# Revit family: Lighting_Pendant-Lighting_Molto-Luce_Log-Out-2-1-Bina-Lens-Recessed_999
name_source: partatom
category: Lighting Fixtures
revit_build: Autodesk Revit 2018 (Build: 20170223_1515(x64)
units: mm (PartAtom-declared; Revit-internal decimal feet)

## family parameters
Cut with Voids When Loaded = No
Host = Face
Light Source = Yes
OmniClass Number = 23.80.70.00
OmniClass Title = Lighting
Part Type = Normal
Room Calculation Point = No
Round Connector Dimension = Use Diameter
Shared = No

## types (54) — shared parameters
BIMobject category = Pendant Lighting
Color Filter = 16777215
Default Elevation = 1219 mm
Design country = Austria
Dimming Lamp Color Temperature Shift = <None>
Edition number = 1
IFC Classification = Lamp
Installation instructions = https://www.moltoluce.com
Light Source Symbol Size = 610 mm
Manufacturer = Molto Luce
Manufacturer country = Austria
Manufacturer name = Molto Luce
Masterformat 2014 Code = 26 50 00
Masterformat 2014 Description = Lighting
Material main = Aluminium
Material secondary = Acrylic
Model = Log Out 2.1 Bina Lens Recessed
NBS Reference Code = 49
NBS Reference Description = Luminaires And Lamps
OmniClass Code = 23-35 45 15
OmniClass Description = Lamps
Product Guid = 61130c55-a570-4c15-9c05-078dfd1a0b47
Product SKU = Log_Out_2_1_Bina_Lens_Recessed
Product data url = https://bimobject.com
Product family = Lighting
Product group = Pendant Lamp
Product name = Log Out 2.1 Bina Lens Recessed
Product url = https://www.moltoluce.com
QR code = https://bimobject.com
UNSPSC Code = 3911
URL = https://www.moltoluce.com
Uniclass 1.4 Code = JY73
Uniclass 1.4 Description = Luminaires and lamps
Uniclass 2.0 Code = PR-49
Uniclass 2.0 Description = Luminaires And Lamps
Uniclass 2015 Code = Pr_70_70_48
Uniclass 2015 Name = Luminaires, lighting track and lighting accessories
Uniformat II Code = D5020
Uniformat II Description = Lighting & Branch Wiring

## per-type parameters (varying)
| type | Description | Emit from Line Length | Housing Color | Length 1131 mm | Length 2255 mm | Length 3379 mm | Light Location |
| Length 1131 mm 43W - CRI > 80 - Color temperature 4000K - Housing Color Natural Anodised - DALI | LOG OUT 2.1 & LOG IN 2.1 are available as pendant, surface-mounted and recessed luminaires. The profile is made of extruded aluminium and is available in black, white and aluminium-coloured surfaces. Due to its simple, straightforward look, the LOG series can be integrated discretely, yet distinctively into any style of architecture as a great lighting solution. The modular system offers additional components which can be perfectly combined with the profile. The lighting inserts with opal cover or microprismatic foil as well as the new BINA inserts which are available as UGR<19 and as ball-proof version, are just perfect as basic lighting. The Trigga insert and the MOVA spotlight can be used as additional lighting elements for the LOG OUT 2.1, LOG IN 2.1 & LOG IN TRIMLESS 2.1 system. | 1131 mm  [stored 3.71063 ft] | Molto Luce - Natural Anodised | Yes | No | No | 524 mm |
| Length 3379 mm 129W - CRI > 80 - Color temperature 4000K - Housing Color Natural Anodised - DALI |  | 3379 mm  [stored 11.086 ft] | Molto Luce - Natural Anodised | No | No | Yes | 1648 mm |
| Length 2255 mm 86W - CRI > 80 - Color temperature 4000K - Housing Color Natural Anodised - DALI |  | 2255 mm  [stored 7.39829 ft] | Molto Luce - Natural Anodised | No | Yes | No | 1086 mm |
| Length 1131 mm 43W - CRI > 80 - Color temperature 3000K - Housing Color Natural Anodised - DALI |  | 1131 mm  [stored 3.71063 ft] | Molto Luce - Natural Anodised | Yes | No | No | 524 mm |
| Length 3379 mm 129W - CRI > 80 - Color temperature 3000K - Housing Color Natural Anodised - DALI |  | 3379 mm  [stored 11.086 ft] | Molto Luce - Natural Anodised | No | No | Yes | 1648 mm |
| Length 2255 mm 86W - CRI > 80 - Color temperature 3000K - Housing Color Natural Anodised - DALI |  | 2255 mm  [stored 7.39829 ft] | Molto Luce - Natural Anodised | No | Yes | No | 1086 mm |
| Length 1131 mm 43W - CRI > 80 - Color temperature 2700K - Housing Color Natural Anodised - DALI |  | 1131 mm  [stored 3.71063 ft] | Molto Luce - Natural Anodised | Yes | No | No | 524 mm |
| Length 3379 mm 129W - CRI > 80 - Color temperature 2700K - Housing Color Natural Anodised - DALI |  | 3379 mm  [stored 11.086 ft] | Molto Luce - Natural Anodised | No | No | Yes | 1648 mm |
| Length 2255 mm 86W - CRI > 80 - Color temperature 2700K - Housing Color Natural Anodised - DALI |  | 2255 mm  [stored 7.39829 ft] | Molto Luce - Natural Anodised | No | Yes | No | 1086 mm |
| Length 1131 mm 43W - CRI > 80 - Color temperature 4000K - Housing Color White - DALI |  | 1131 mm  [stored 3.71063 ft] | Molto Luce - White | Yes | No | No | 524 mm |
| Length 3379 mm 129W - CRI > 80 - Color temperature 4000K - Housing Color White - DALI |  | 3379 mm  [stored 11.086 ft] | Molto Luce - White | No | No | Yes | 1648 mm |
| Length 2255 mm 86W - CRI > 80 - Color temperature 4000K - Housing Color White - DALI |  | 2255 mm  [stored 7.39829 ft] | Molto Luce - White | No | Yes | No | 1086 mm |
| Length 1131 mm 43W - CRI > 80 - Color temperature 3000K - Housing Color White - DALI |  | 1131 mm  [stored 3.71063 ft] | Molto Luce - White | Yes | No | No | 524 mm |
| Length 3379 mm 129W - CRI > 80 - Color temperature 3000K - Housing Color White - DALI |  | 3379 mm  [stored 11.086 ft] | Molto Luce - White | No | No | Yes | 1648 mm |
| Length 2255 mm 86W - CRI > 80 - Color temperature 3000K - Housing Color White - DALI |  | 2255 mm  [stored 7.39829 ft] | Molto Luce - White | No | Yes | No | 1086 mm |
| Length 1131 mm 43W - CRI > 80 - Color temperature 2700K - Housing Color White - DALI |  | 1131 mm  [stored 3.71063 ft] | Molto Luce - White | Yes | No | No | 524 mm |
| Length 3379 mm 129W - CRI > 80 - Color temperature 2700K - Housing Color White - DALI |  | 3379 mm  [stored 11.086 ft] | Molto Luce - White | No | No | Yes | 1648 mm |
| Length 2255 mm 86W - CRI > 80 - Color temperature 2700K - Housing Color White - DALI |  | 2255 mm  [stored 7.39829 ft] | Molto Luce - White | No | Yes | No | 1086 mm |
| Length 1131 mm 43W - CRI > 80 - Color temperature 4000K - Housing Color Black - DALI |  | 1131 mm  [stored 3.71063 ft] | Molto Luce - Black | Yes | No | No | 524 mm |
| Length 3379 mm 129W - CRI > 80 - Color temperature 4000K - Housing Color Black - DALI |  | 3379 mm  [stored 11.086 ft] | Molto Luce - Black | No | No | Yes | 1648 mm |
| Length 2255 mm 86W - CRI > 80 - Color temperature 4000K - Housing Color Black - DALI |  | 2255 mm  [stored 7.39829 ft] | Molto Luce - Black | No | Yes | No | 1086 mm |
| Length 1131 mm 43W - CRI > 80 - Color temperature 3000K - Housing Color Black - DALI |  | 1131 mm  [stored 3.71063 ft] | Molto Luce - Black | Yes | No | No | 524 mm |
| Length 3379 mm 129W - CRI > 80 - Color temperature 3000K - Housing Color Black - DALI |  | 3379 mm  [stored 11.086 ft] | Molto Luce - Black | No | No | Yes | 1648 mm |
| Length 2255 mm 86W - CRI > 80 - Color temperature 3000K - Housing Color Black - DALI |  | 2255 mm  [stored 7.39829 ft] | Molto Luce - Black | No | Yes | No | 1086 mm |
| Length 1131 mm 43W - CRI > 80 - Color temperature 2700K - Housing Color Black - DALI |  | 1131 mm  [stored 3.71063 ft] | Molto Luce - Black | Yes | No | No | 524 mm |
| Length 3379 mm 129W - CRI > 80 - Color temperature 2700K - Housing Color Black - DALI |  | 3379 mm  [stored 11.086 ft] | Molto Luce - Black | No | No | Yes | 1648 mm |
| Length 2255 mm 86W - CRI > 80 - Color temperature 2700K - Housing Color Black - DALI |  | 2255 mm  [stored 7.39829 ft] | Molto Luce - Black | No | Yes | No | 1086 mm |
| Length 1131 mm 43W - CRI > 80 - Color temperature 4000K - Housing Color Natural Anodised |  | 1131 mm  [stored 3.71063 ft] | Molto Luce - Natural Anodised | Yes | No | No | 524 mm |
| Length 3379 mm 129W - CRI > 80 - Color temperature 4000K - Housing Color Natural Anodised |  | 3379 mm  [stored 11.086 ft] | Molto Luce - Natural Anodised | No | No | Yes | 1648 mm |
| Length 2255 mm 86W - CRI > 80 - Color temperature 4000K - Housing Color Natural Anodised |  | 2255 mm  [stored 7.39829 ft] | Molto Luce - Natural Anodised | No | Yes | No | 1086 mm |
| Length 1131 mm 43W - CRI > 80 - Color temperature 3000K - Housing Color Natural Anodised |  | 1131 mm  [stored 3.71063 ft] | Molto Luce - Natural Anodised | Yes | No | No | 524 mm |
| Length 3379 mm 129W - CRI > 80 - Color temperature 3000K - Housing Color Natural Anodised |  | 3379 mm  [stored 11.086 ft] | Molto Luce - Natural Anodised | No | No | Yes | 1648 mm |
| Length 2255 mm 86W - CRI > 80 - Color temperature 3000K - Housing Color Natural Anodised |  | 2255 mm  [stored 7.39829 ft] | Molto Luce - Natural Anodised | No | Yes | No | 1086 mm |
| Length 1131 mm 43W - CRI > 80 - Color temperature 2700K - Housing Color Natural Anodised |  | 1131 mm  [stored 3.71063 ft] | Molto Luce - Natural Anodised | Yes | No | No | 524 mm |
| Length 3379 mm 129W - CRI > 80 - Color temperature 2700K - Housing Color Natural Anodised |  | 3379 mm  [stored 11.086 ft] | Molto Luce - Natural Anodised | No | No | Yes | 1648 mm |
| Length 2255 mm 86W - CRI > 80 - Color temperature 2700K - Housing Color Natural Anodised |  | 2255 mm  [stored 7.39829 ft] | Molto Luce - Natural Anodised | No | Yes | No | 1086 mm |
| Length 1131 mm 43W - CRI > 80 - Color temperature 4000K - Housing Color White |  | 1131 mm  [stored 3.71063 ft] | Molto Luce - White | Yes | No | No | 524 mm |
| Length 3379 mm 129W - CRI > 80 - Color temperature 4000K - Housing Color White |  | 3379 mm  [stored 11.086 ft] | Molto Luce - White | No | No | Yes | 1648 mm |
| Length 2255 mm 86W - CRI > 80 - Color temperature 4000K - Housing Color White |  | 2255 mm  [stored 7.39829 ft] | Molto Luce - White | No | Yes | No | 1086 mm |
| Length 1131 mm 43W - CRI > 80 - Color temperature 3000K - Housing Color White |  | 1131 mm  [stored 3.71063 ft] | Molto Luce - White | Yes | No | No | 524 mm |
| Length 3379 mm 129W - CRI > 80 - Color temperature 3000K - Housing Color White |  | 3379 mm  [stored 11.086 ft] | Molto Luce - White | No | No | Yes | 1648 mm |
| Length 2255 mm 86W - CRI > 80 - Color temperature 3000K - Housing Color White |  | 2255 mm  [stored 7.39829 ft] | Molto Luce - White | No | Yes | No | 1086 mm |
| Length 1131 mm 43W - CRI > 80 - Color temperature 2700K - Housing Color White |  | 1131 mm  [stored 3.71063 ft] | Molto Luce - White | Yes | No | No | 524 mm |
| Length 3379 mm 129W - CRI > 80 - Color temperature 2700K - Housing Color White |  | 3379 mm  [stored 11.086 ft] | Molto Luce - White | No | No | Yes | 1648 mm |
| Length 2255 mm 86W - CRI > 80 - Color temperature 2700K - Housing Color White |  | 2255 mm  [stored 7.39829 ft] | Molto Luce - White | No | Yes | No | 1086 mm |
| Length 1131 mm 43W - CRI > 80 - Color temperature 4000K - Housing Color Black |  | 1131 mm  [stored 3.71063 ft] | Molto Luce - Black | Yes | No | No | 524 mm |
| Length 3379 mm 129W - CRI > 80 - Color temperature 4000K - Housing Color Black |  | 3379 mm  [stored 11.086 ft] | Molto Luce - Black | No | No | Yes | 1648 mm |
| Length 2255 mm 86W - CRI > 80 - Color temperature 4000K - Housing Color Black |  | 2255 mm  [stored 7.39829 ft] | Molto Luce - Black | No | Yes | No | 1086 mm |
| Length 1131 mm 43W - CRI > 80 - Color temperature 3000K - Housing Color Black |  | 1131 mm  [stored 3.71063 ft] | Molto Luce - Black | Yes | No | No | 524 mm |
| Length 3379 mm 129W - CRI > 80 - Color temperature 3000K - Housing Color Black |  | 3379 mm  [stored 11.086 ft] | Molto Luce - Black | No | No | Yes | 1648 mm |
| Length 2255 mm 86W - CRI > 80 - Color temperature 3000K - Housing Color Black |  | 2255 mm  [stored 7.39829 ft] | Molto Luce - Black | No | Yes | No | 1086 mm |
| Length 1131 mm 43W - CRI > 80 - Color temperature 2700K - Housing Color Black |  | 1131 mm  [stored 3.71063 ft] | Molto Luce - Black | Yes | No | No | 524 mm |
| Length 3379 mm 129W - CRI > 80 - Color temperature 2700K - Housing Color Black |  | 3379 mm  [stored 11.086 ft] | Molto Luce - Black | No | No | Yes | 1648 mm |
| Length 2255 mm 86W - CRI > 80 - Color temperature 2700K - Housing Color Black |  | 2255 mm  [stored 7.39829 ft] | Molto Luce - Black | No | Yes | No | 1086 mm |

note: [stored X ft] marks values corroborated as IEEE doubles in the binary element streams (Revit-internal decimal feet)

## geometry (parser evidence)
native form markers: Sweep x6
no freeform markers — native parametric forms only
